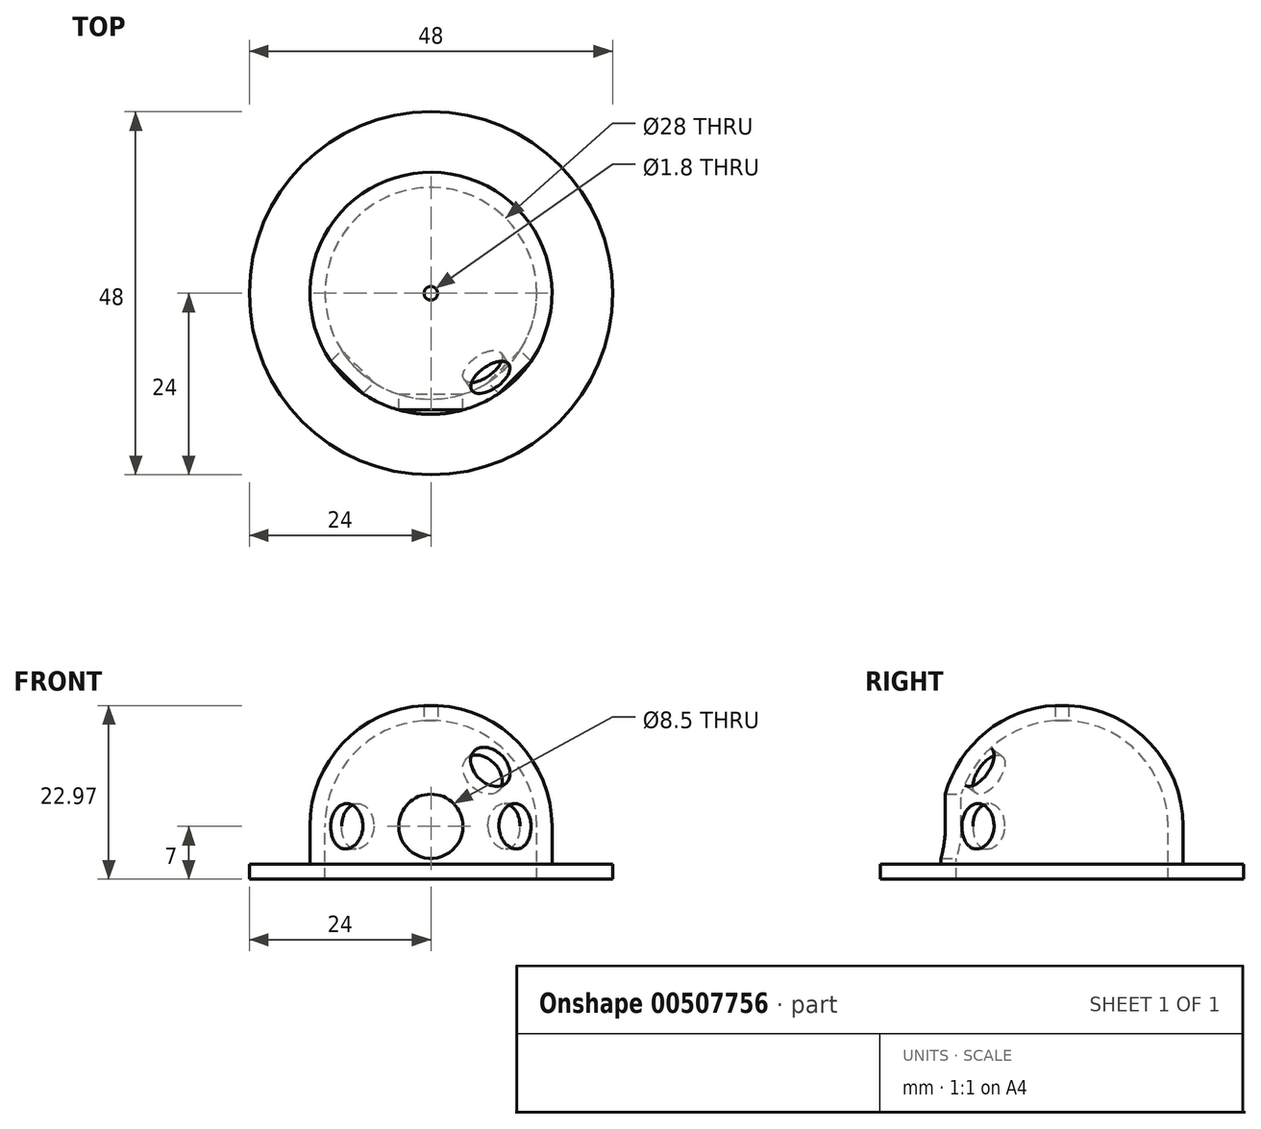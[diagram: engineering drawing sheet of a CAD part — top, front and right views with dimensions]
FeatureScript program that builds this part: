
annotation { "Feature Type Name" : "Feature", "Feature Type Description" : "" }
export const myFeature = defineFeature(function(context is Context, id is Id, definition is map)
    precondition{}
    {
        {
            var Q0;
            Q0=qCreatedBy(makeId("Front.planeOp"),FACE);
            var sketch = newSketch(context, id + "F0", { "sketchPlane" : qUnion([Q0])});
            skLineSegment(sketch, "E0", {"start": v(-14, -7) * mm, "end": v(-24, -7) * mm});
            skLineSegment(sketch, "E1", {"start": v(-24, -7) * mm, "end": v(-24, -5) * mm});
            skLineSegment(sketch, "E2", {"start": v(-24, -5) * mm, "end": v(-16, -5) * mm});
            skLineSegment(sketch, "E3", {"start": v(-16, -5) * mm, "end": v(-16, 0) * mm});
            skLineSegment(sketch, "E4", {"start": v(-14, -7) * mm, "end": v(-14, 0) * mm});
            skArc(sketch, "E5", {"start": v(0, 14) * mm, "mid": v(-9.9, 9.9) * mm, "end": v(-14, 0) * mm});
            skArc(sketch, "E6", {"start": v(0, 16) * mm, "mid": v(-11.31, 11.31) * mm, "end": v(-16, 0) * mm});
            skLineSegment(sketch, "E7", {"start": v(0, 16) * mm, "end": v(0, 14) * mm});
            skSolve(sketch);
        }
        {
            var Q0;
            Q0=qSketchRegion(id+"F0",true);
            var Q1;
            Q1=sQuery(id+"F0.wireOp",EDGE,"E7");
            revolve(context, id + "F1", {"entities" : qUnion([Q0]), "axis" : qUnion([Q1]), "revolveType" : RevolveType.FULL});
        }
        {
            var Q0;
            Q0=qCreatedBy(makeId("Front.planeOp"),FACE);
            var sketch = newSketch(context, id + "F2", { "sketchPlane" : qUnion([Q0])});
            skCircle(sketch, "E8", {"center": v(0, 0) * mm, "radius": 4.25 * mm});
            skSolve(sketch);
        }
        {
            var Q0;
            Q0=qSketchRegion(id+"F2",true);
            extrude(context, id + "F3", {"entities" : qUnion([Q0]), "operationType" : NewBodyOperationType.REMOVE, "depth" : 50 * mm});
        }
        {
            var Q0;
            Q0=qCreatedBy(makeId("Top.planeOp"),FACE);
            var sketch = newSketch(context, id + "F4", { "sketchPlane" : qUnion([Q0])});
            skLineSegment(sketch, "E9", {"start": v(-39.11, -39.11) * mm, "end": v(32.62, 32.62) * mm, "construction": true});
            skLineSegment(sketch, "E10", {"start": v(-37.35, 37.35) * mm, "end": v(42.98, -42.98) * mm, "construction": true});
            skSolve(sketch);
        }
        {
            var Q0;
            Q0=sQuery(id+"F4.wireOp",EDGE,"E10");
            cPlane(context, id + "F5", {"entities" : qUnion([Q0]), "cplaneType" : CPlaneType.LINE_ANGLE, "offset" : 25 * mm, "angle" : 90 * degree, "width" : 150 * mm, "height" : 150 * mm});
        }
        {
            var Q0;
            Q0=qCreatedBy(id+"F5.planeOp",FACE);
            var sketch = newSketch(context, id + "F6", { "sketchPlane" : qUnion([Q0])});
            skCircle(sketch, "E11", {"center": v(0, 0) * mm, "radius": 3 * mm});
            skSolve(sketch);
        }
        {
            var Q0;
            Q0=qSketchRegion(id+"F6",true);
            extrude(context, id + "F7", {"entities" : qUnion([Q0]), "operationType" : NewBodyOperationType.REMOVE, "oppositeDirection" : true, "depth" : 25 * mm});
        }
        {
            var Q0;
            Q0=qCreatedBy(makeId("Front.planeOp"),FACE);
            var sketch = newSketch(context, id + "F8", { "sketchPlane" : qUnion([Q0])});
            skLineSegment(sketch, "E12", {"start": v(0, 0) * mm, "end": v(30.29, 30.29) * mm, "construction": true});
            skLineSegment(sketch, "E13", {"start": v(0, 0) * mm, "end": v(-31.13, 31.13) * mm, "construction": true});
            skSolve(sketch);
        }
        {
            var Q0;
            Q0=sQuery(id+"F8.wireOp",EDGE,"E12");
            cPlane(context, id + "F9", {"entities" : qUnion([Q0]), "cplaneType" : CPlaneType.LINE_ANGLE, "offset" : 25 * mm, "angle" : 90 * degree, "width" : 150 * mm, "height" : 150 * mm});
        }
        {
            var Q0;
            Q0=qCreatedBy(id+"F9.planeOp",FACE);
            var sketch = newSketch(context, id + "F10", { "sketchPlane" : qUnion([Q0])});
            skLineSegment(sketch, "E14", {"start": v(0, 0) * mm, "end": v(19.81, 19.81) * mm, "construction": true});
            skLineSegment(sketch, "E15", {"start": v(16.68, 16.68) * mm, "end": v(14.56, 18.8) * mm});
            skLineSegment(sketch, "E16", {"start": v(14.56, 18.8) * mm, "end": v(1.88, 6.12) * mm});
            skLineSegment(sketch, "E17", {"start": v(1.88, 6.12) * mm, "end": v(4, 4) * mm});
            skLineSegment(sketch, "E18", {"start": v(4, 4) * mm, "end": v(16.68, 16.68) * mm});
            skSolve(sketch);
        }
        {
            var Q0;
            Q0=qSketchRegion(id+"F10",true);
            var Q1;
            Q1=sQuery(id+"F10.wireOp",EDGE,"E18");
            revolve(context, id + "F11", {"operationType" : NewBodyOperationType.REMOVE, "entities" : qUnion([Q0]), "axis" : qUnion([Q1]), "revolveType" : RevolveType.FULL, "oppositeDirection" : true});
        }
        {
            var Q0;
            Q0=sQuery(id+"F4.wireOp",EDGE,"E9");
            cPlane(context, id + "F12", {"entities" : qUnion([Q0]), "cplaneType" : CPlaneType.LINE_ANGLE, "offset" : 25 * mm, "angle" : 90 * degree, "width" : 150 * mm, "height" : 150 * mm});
        }
        {
            var Q0;
            Q0=qCreatedBy(id+"F12.planeOp",FACE);
            var sketch = newSketch(context, id + "F13", { "sketchPlane" : qUnion([Q0])});
            skCircle(sketch, "E19", {"center": v(0, 0) * mm, "radius": 3 * mm});
            skSolve(sketch);
        }
        {
            var Q0;
            Q0=qSketchRegion(id+"F13",true);
            extrude(context, id + "F14", {"entities" : qUnion([Q0]), "operationType" : NewBodyOperationType.REMOVE, "depth" : 25 * mm});
        }
        {
            var Q0;
            Q0=sQuery(id+"F8.wireOp",EDGE,"E13");
            cPlane(context, id + "F15", {"entities" : qUnion([Q0]), "cplaneType" : CPlaneType.LINE_ANGLE, "offset" : 25 * mm, "angle" : 90 * degree, "width" : 150 * mm, "height" : 150 * mm});
        }
        {
            var Q0;
            Q0=qCreatedBy(makeId("Top.planeOp"),FACE);
            var sketch = newSketch(context, id + "F16", { "sketchPlane" : qUnion([Q0])});
            skCircle(sketch, "E20", {"center": v(0, 0) * mm, "radius": 0.9 * mm});
            skSolve(sketch);
        }
        {
            var Q0;
            Q0=qSketchRegion(id+"F16",true);
            extrude(context, id + "F17", {"entities" : qUnion([Q0]), "operationType" : NewBodyOperationType.REMOVE, "depth" : 30.1 * mm});
        }
        {
            var Q0;
            Q0=qCreatedBy(makeId("Right.planeOp"),FACE);
            var sketch = newSketch(context, id + "F18", { "sketchPlane" : qUnion([Q0])});
            skLineSegment(sketch, "E21", {"start": v(-34.54, 0) * mm, "end": v(39.7, 0) * mm, "construction": true});
            skSolve(sketch);
        }
        {
            var Q0;
            Q0=qCreatedBy(makeId("Top.planeOp"),FACE);
            var sketch = newSketch(context, id + "F19", { "sketchPlane" : qUnion([Q0])});
            skLineSegment(sketch, "E22", {"start": v(0, 0) * mm, "end": v(0, -71.29) * mm, "construction": true});
            skSolve(sketch);
        }
    });
